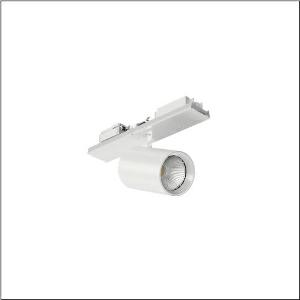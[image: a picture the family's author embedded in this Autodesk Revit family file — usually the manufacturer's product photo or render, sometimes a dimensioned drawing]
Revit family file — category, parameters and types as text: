
# Revit family: licross_spot_31_51sl127a45b
name_source: partatom
category: Lighting Fixtures
units: mm (PartAtom-declared; Revit-internal decimal feet)

## family parameters
Cut with Voids When Loaded = No
Host = Face
Light Source = No
Part Type = Normal
Room Calculation Point = No
Round Connector Dimension = Use Diameter
Shared = No

## types (1)
- --- (1 x LED, 5140 lm, 42.6 W, 4000K)
    Apparent Load = 43 VA
    CIE Flux Codes = 93 97 99 100 100
    Color Rendering = 90
    Color Temperature = 4000K
    Default Elevation = 1800 mm
    Description = Licross Spot 31, directional spotlight, light control with lens, of plastic, LED rated luminous flux: 5.140lm, light colour: 940, with plug, 3-pole, with phase selection, mains connection: 220..240V, AC, 50/60Hz, of aluminium, traffic white (RAL 9016), length: 300mm, diameter: 90mm, protection rating (complete): IP20, insulation class (complete): insulation class I (protective earthing), certification: CE, packaging unit: 1 piece
    Height = 175 mm
    Lamp = 1 x LED
    Lamp Light Flux = 5140 lm
    Lamp Power = 42.6 W
    Lamp count = 1
    Length = 90 mm
    Luminous efficacy = 121 lm/W
    Manufacturer = Siteco
    ModVariant = No
    Model = 51SL127A45B
    Mounting Place = Ceiling
    Mounting Type = Pendant
    Number of Poles = 1
    OnlyDefault = Yes
    Power Factor = 1
    Product Name = Licross Spot 31
    Product group = directional spotlight
    ProductGroupID = 905
    Protection Class = Protection class I
    Protection Degree = IP 20
    RLX_Detail_Level = 1
    RLX_Emergency_Light_Flux = 0 lm
    RLX_Emergency_Type = 0
    RLX_Emergency_Type_DB = No
    RlxData = <blob elided: 14777 chars, md5=f03e01c5>
    Socket = socket
    Standby Power = 0 W
    System Light Flux = 5140 lm
    System Power = 43 W
    Type Comments = factory setting: luminous flux: 100 % | (ON | ON | ON) | 1050 mA
    Type Image = l_1245720.jpg
    URL = http://relux.com
    VarID = @adj_133805
    Voltage = 0 V
    Weight = 0.00 kg
    Width = 0 mm  [stored 0 ft]

note: [stored X ft] marks values corroborated as IEEE doubles in the binary element streams (Revit-internal decimal feet)

## geometry (parser evidence)
native form markers: Sweep x13
no freeform markers — native parametric forms only
